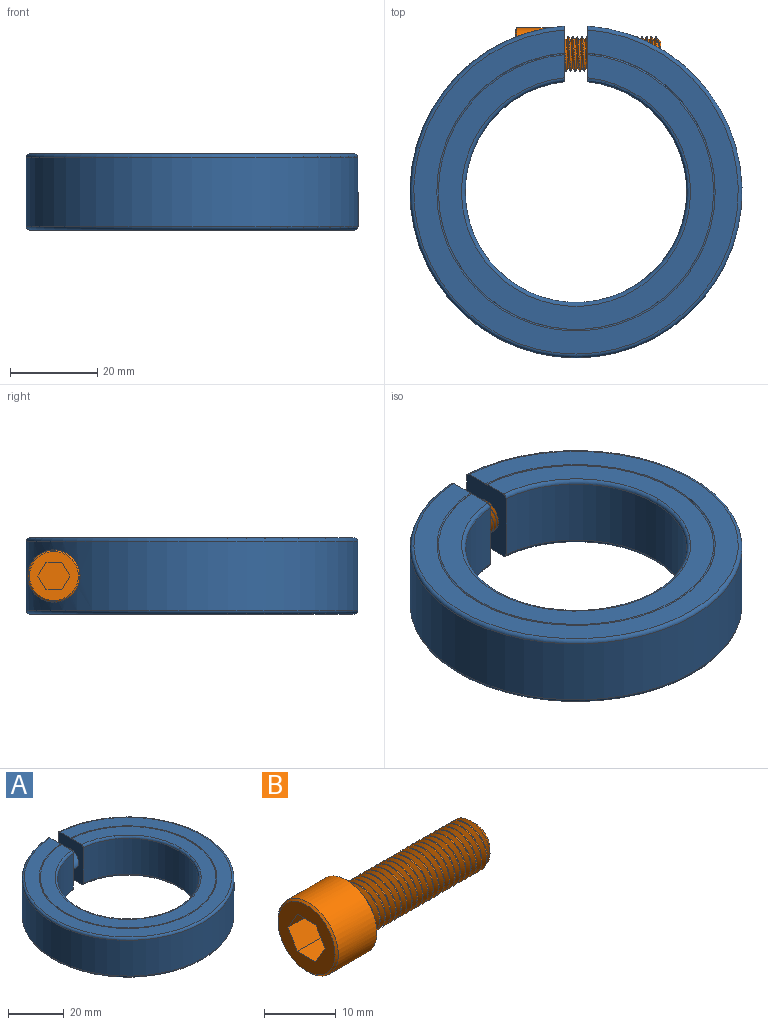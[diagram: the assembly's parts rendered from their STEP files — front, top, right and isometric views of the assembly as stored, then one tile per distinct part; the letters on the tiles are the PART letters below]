
ASSEMBLY  parts=2 mates=1
PART A: 16 faces, bbox 82.5x82.4x17.5 mm
  f0: cylinder r=3.97mm len=7.94mm, axis (1,0,0), area 85.1mm2, adj f10,f15
  f1: cylinder r=6.02mm len=22.25mm, axis (1,0,0), area 512.2mm2, adj f9,f15
  f2: cylinder r=3.97mm len=23.65mm, axis (1,0,0), area 449.2mm2, adj f9,f11
  f3: torus R=31.75mm, axis (0,0,-1), area 116.3mm2, adj f10,f11,f12,f13
  f4: torus R=26.27mm, axis (0,0,1), area 214.7mm2, adj f8,f10,f11,f14
  f5: torus R=26.27mm, axis (0,0,1), area 214.7mm2, adj f8,f10,f11,f13
  f6: torus R=37.23mm, axis (0,0,1), area 318.6mm2, adj f9,f10,f11,f14
  f7: torus R=37.23mm, axis (0,0,1), area 318.6mm2, adj f9,f10,f11,f12
  f8: cylinder r=25.4mm len=50.8mm, axis (0,0,-1), area 2428.2mm2, adj f4,f5,f10,f11
  f9: cylinder r=38.1mm len=76.2mm, axis (0,0,-1), area 3360.4mm2, adj f1,f2,f6,f7,f10,f11,f15
  f10: plane 17.5x12.78mm, normal (1,0,0), area 172.3mm2, adj f0,f3,f4,f5,f6,f7,f8,f9
  f11: plane 17.5x12.78mm, normal (-1,0,0), area 172.3mm2, adj f2,f3,f4,f5,f6,f7,f8,f9
  f12: plane 74.45x74.37mm, normal (0,0,1), area 1121.8mm2, adj f3,f7,f10,f11
  f13: plane 63.12x63.02mm, normal (0,0,1), area 933.6mm2, adj f3,f5,f10,f11
  f14: plane 74.45x74.37mm, normal (0,0,-1), area 2129.5mm2, adj f4,f6,f10,f11
  f15: plane 12.03x12mm, normal (-1,0,0), area 64.2mm2, adj f0,f1,f9
PART B: 41 faces, bbox 33.4x11.9x11.9 mm
  f0: cone r=5.95mm half-angle=45deg, axis (1,0,0), area 16.3mm2, adj f1,f27
  f1: cylinder r=5.95mm len=11.91mm, axis (1,0,0), area 285mm2, adj f0,f28
  f2: cone r=2.91mm half-angle=45deg, axis (-1,0,0), area 18.6mm2, adj f3,f29,f38,f39,f40
  f3: cone r=2.91mm half-angle=45deg, axis (-1,0,0), area 2.4mm2, adj f2,f26,f38,f40
  f4: cylinder r=3.97mm len=7.94mm, axis (1,0,0), area 22.3mm2, adj f5,f28,f37,f38,f40
  f5: cylinder r=3.97mm len=7.94mm, axis (1,0,0), area 3.3mm2, adj f4,f6,f38,f40
  f6: cylinder r=3.97mm len=7.94mm, axis (1,0,0), area 3.3mm2, adj f5,f7,f38,f40
  f7: cylinder r=3.97mm len=7.94mm, axis (1,0,0), area 3.3mm2, adj f6,f8,f38,f40
  f8: cylinder r=3.97mm len=7.94mm, axis (1,0,0), area 3.3mm2, adj f7,f9,f38,f40
  f9: cylinder r=3.97mm len=7.94mm, axis (1,0,0), area 3.3mm2, adj f8,f10,f38,f40
  f10: cylinder r=3.97mm len=7.94mm, axis (1,0,0), area 3.3mm2, adj f9,f11,f38,f40
  f11: cylinder r=3.97mm len=7.94mm, axis (1,0,0), area 3.3mm2, adj f10,f12,f38,f40
  f12: cylinder r=3.97mm len=7.94mm, axis (1,0,0), area 3.3mm2, adj f11,f13,f38,f40
  f13: cylinder r=3.97mm len=7.94mm, axis (1,0,0), area 3.3mm2, adj f12,f14,f38,f40
  f14: cylinder r=3.97mm len=7.94mm, axis (1,0,0), area 3.3mm2, adj f13,f15,f38,f40
  f15: cylinder r=3.97mm len=7.94mm, axis (1,0,0), area 3.3mm2, adj f14,f16,f38,f40
  f16: cylinder r=3.97mm len=7.94mm, axis (1,0,0), area 3.3mm2, adj f15,f17,f38,f40
  f17: cylinder r=3.97mm len=7.94mm, axis (1,0,0), area 3.3mm2, adj f16,f18,f38,f40
  f18: cylinder r=3.97mm len=7.94mm, axis (1,0,0), area 3.3mm2, adj f17,f19,f38,f40
  f19: cylinder r=3.97mm len=7.94mm, axis (1,0,0), area 3.3mm2, adj f18,f20,f38,f40
  f20: cylinder r=3.97mm len=7.94mm, axis (1,0,0), area 3.3mm2, adj f19,f21,f38,f40
  f21: cylinder r=3.97mm len=7.94mm, axis (1,0,0), area 3.3mm2, adj f20,f22,f38,f40
  f22: cylinder r=3.97mm len=7.94mm, axis (1,0,0), area 3.3mm2, adj f21,f23,f38,f40
  f23: cylinder r=3.97mm len=7.94mm, axis (1,0,0), area 3.3mm2, adj f22,f24,f38,f40
  f24: cylinder r=3.97mm len=7.94mm, axis (1,0,0), area 3.3mm2, adj f23,f25,f38,f40
  f25: cylinder r=3.97mm len=7.94mm, axis (1,0,0), area 3.3mm2, adj f24,f26,f38,f40
  f26: cylinder r=3.97mm len=2.81mm, axis (1,0,0), area 0.2mm2, adj f3,f25,f38
  f27: plane 11.27x11.27mm, normal (-1,0,0), area 64.9mm2, adj f0,f30,f31,f32,f33,f34,f35
  f28: plane 11.91x11.91mm, normal (1,0,0), area 61.9mm2, adj f1,f4
  f29: plane 5.82x5.82mm, normal (1,0,0), area 26.6mm2, adj f2
  f30: plane 6.35x3.67mm, normal (0,0,1), area 23.3mm2, adj f27,f31,f35,f36
  f31: plane 6.35x3.18mm, normal (0,-0.87,0.5), area 23.3mm2, adj f27,f30,f32,f36
  f32: plane 6.35x3.18mm, normal (0,-0.87,-0.5), area 23.3mm2, adj f27,f31,f33,f36
  f33: plane 6.35x3.67mm, normal (0,0,-1), area 23.3mm2, adj f27,f32,f34,f36
  f34: plane 6.35x3.18mm, normal (0,0.87,-0.5), area 23.3mm2, adj f27,f33,f35,f36
  f35: plane 6.35x3.18mm, normal (0,0.87,0.5), area 23.3mm2, adj f27,f30,f34,f36
  f36: plane 7.33x6.35mm, normal (-1,0,0), area 34.9mm2, adj f30,f31,f32,f33,f34,f35
  f37: plane 0.93x0.69mm, normal (0,-1,0), area 0.4mm2, adj f4,f38,f39,f40
  f38: bspline ~24.63x7.94mm, area 405.4mm2, adj f2,f3,f4,f5,f6,f7,f8,f9
  f39: cylinder r=3.28mm len=24.37mm, axis (-1,0,0), area 67.7mm2, adj f2,f37,f38,f40
  f40: bspline ~24.9x8.05mm, area 413.2mm2, adj f2,f3,f4,f5,f6,f7,f8,f9
PLACE A t=(7.15,-26.98,2.2)mm
PLACE B t=(7.15,-26.98,2.2)mm
MATE fastened B.f0 <-> A.f0  axis (1,0,0) through (1.2,4.67,2.2)mm
